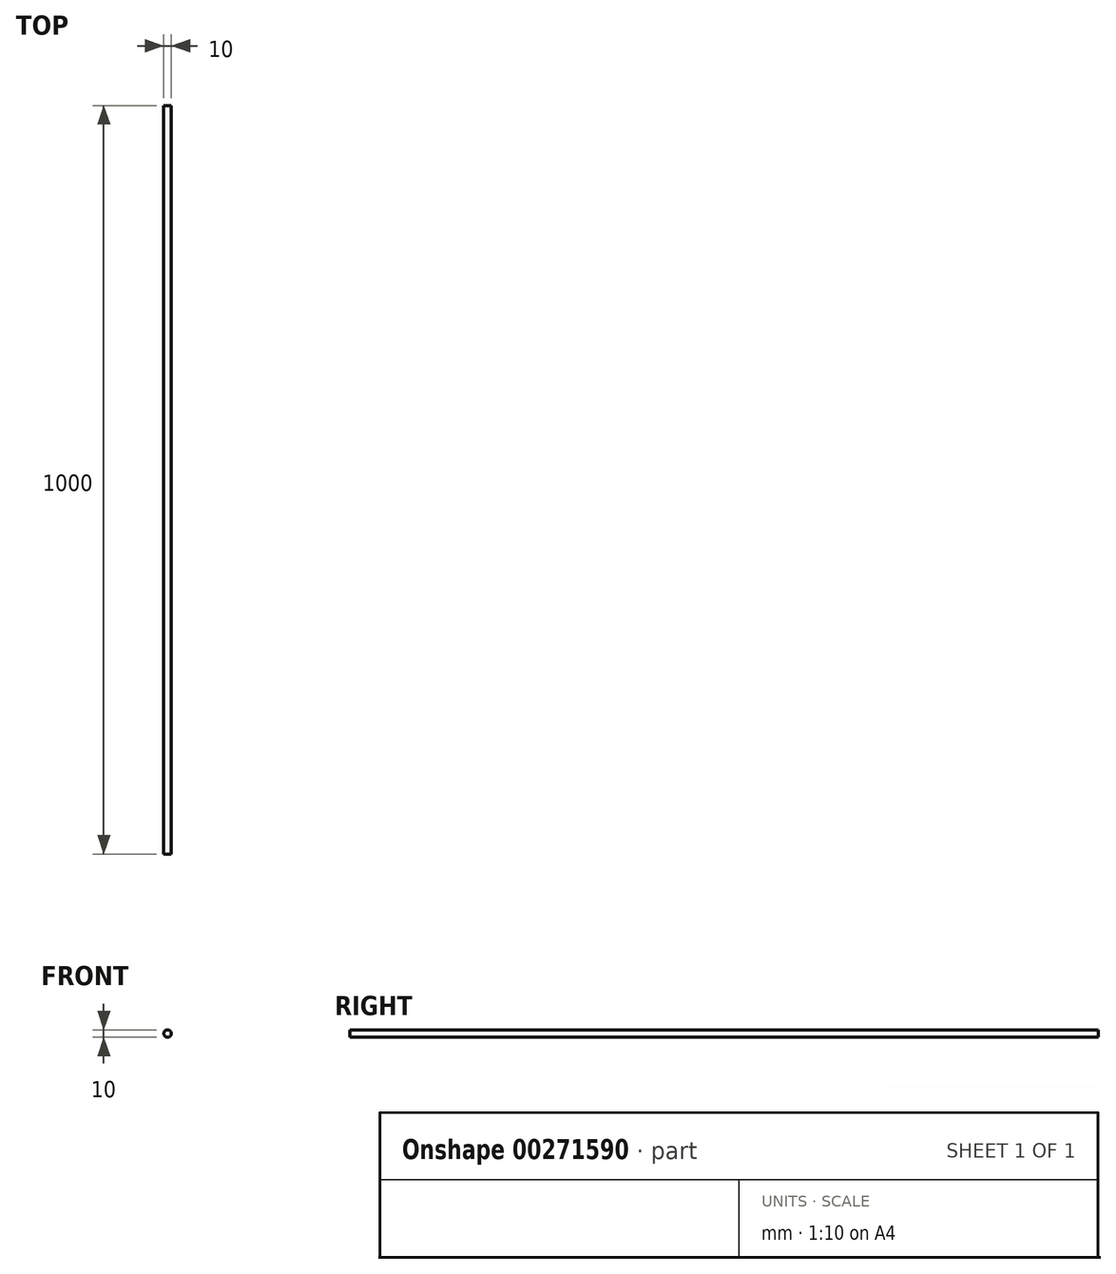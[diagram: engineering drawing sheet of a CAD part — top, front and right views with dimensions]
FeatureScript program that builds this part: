
annotation { "Feature Type Name" : "Feature", "Feature Type Description" : "" }
export const myFeature = defineFeature(function(context is Context, id is Id, definition is map)
    precondition{}
    {
        {
            var Q0;
            Q0=qCreatedBy(makeId("Front.planeOp"),FACE);
            var sketch = newSketch(context, id + "F0", { "sketchPlane" : qUnion([Q0])});
            skCircle(sketch, "E0", {"center": v(0, 0) * mm, "radius": 5 * mm});
            skSolve(sketch);
        }
        {
            var Q0;
            Q0=makeQuery(id+"F0.imprint","IMPRINT",FACE,{"disambiguationData":[TD([[makeQuery(id+"F0.imprint","IMPRINT",EDGE,{"derivedFrom":sQuery(id+"F0.wireOp",EDGE,"E0")}),1.0]])]});
            extrude(context, id + "F1", {"entities" : qUnion([Q0]), "depth" : 1000 * mm});
        }
    });
